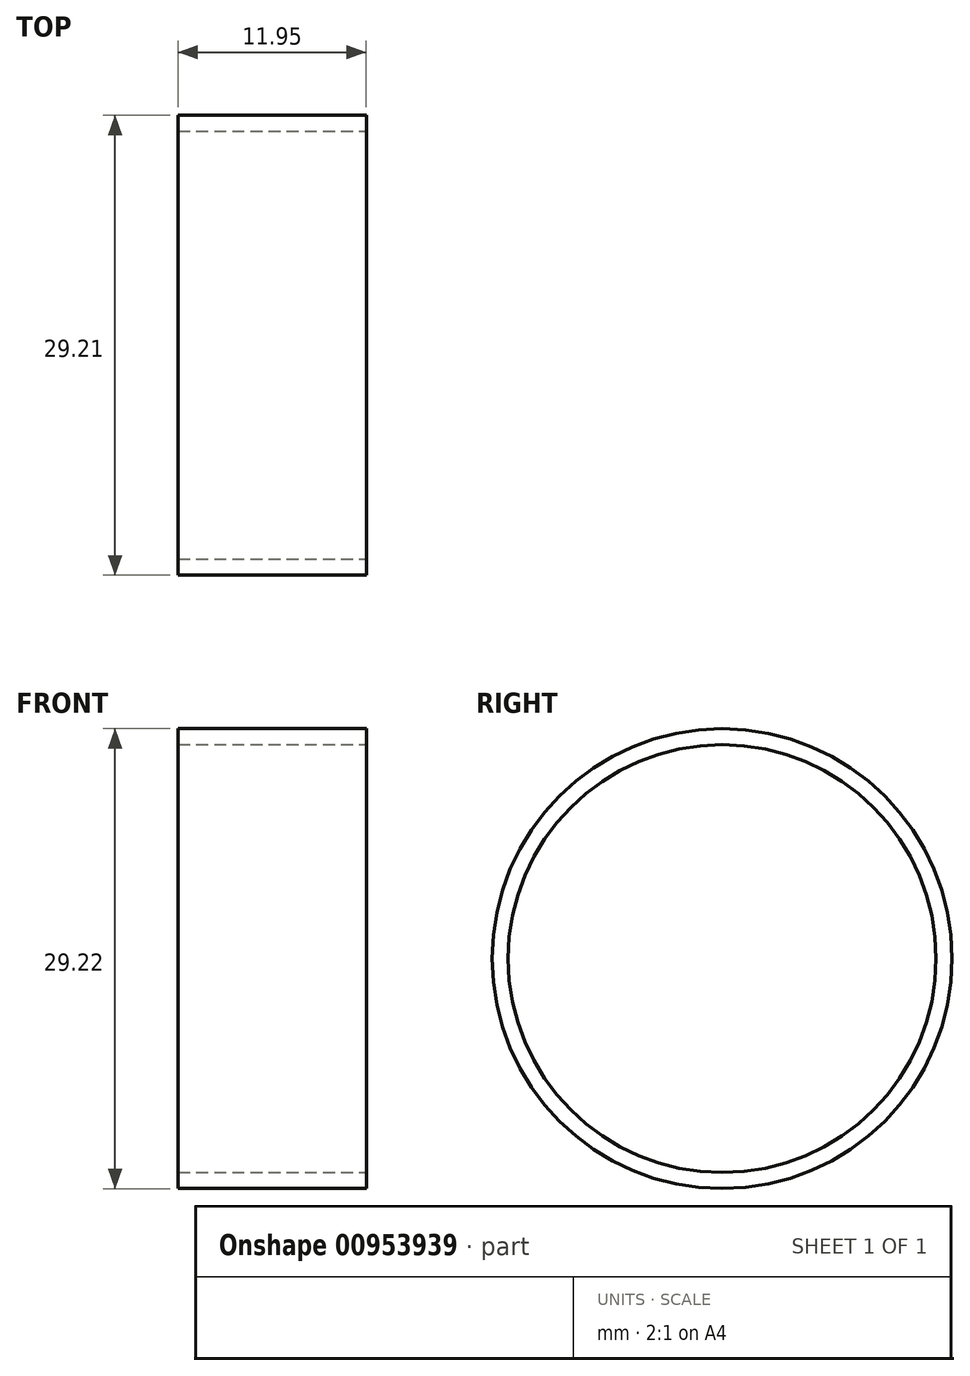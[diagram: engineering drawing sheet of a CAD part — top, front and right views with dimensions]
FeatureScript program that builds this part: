
annotation { "Feature Type Name" : "Feature", "Feature Type Description" : "" }
export const myFeature = defineFeature(function(context is Context, id is Id, definition is map)
    precondition{}
    {
        {
            var Q0;
            Q0=qCreatedBy(makeId("Top.planeOp"),FACE);
            var sketch = newSketch(context, id + "F0", { "sketchPlane" : qUnion([Q0])});
            skLineSegment(sketch, "E0.bottom", {"start": v(-26.7, -2.5) * mm, "end": v(-64.02, -2.5) * mm});
            skLineSegment(sketch, "E0.top", {"start": v(-26.7, -31.7) * mm, "end": v(-64.02, -31.7) * mm});
            skLineSegment(sketch, "E0.left", {"start": v(-26.7, -2.5) * mm, "end": v(-26.7, -31.7) * mm});
            skLineSegment(sketch, "E0.right", {"start": v(-64.02, -2.5) * mm, "end": v(-64.02, -31.7) * mm});
            skLineSegment(sketch, "E1", {"start": v(-26.7, -17.1) * mm, "end": v(-64.02, -17.1) * mm, "construction": true});
            skLineSegment(sketch, "E2.bottom", {"start": v(-64.02, -2.5) * mm, "end": v(-52.07, -2.5) * mm});
            skLineSegment(sketch, "E2.top", {"start": v(-64.02, -3.5) * mm, "end": v(-52.07, -3.5) * mm});
            skLineSegment(sketch, "E2.left", {"start": v(-64.02, -2.5) * mm, "end": v(-64.02, -3.5) * mm});
            skLineSegment(sketch, "E2.right", {"start": v(-52.07, -2.5) * mm, "end": v(-52.07, -3.5) * mm});
            skSolve(sketch);
        }
        {
            var Q0;
            {var subQ4=sQuery(id+"F0.wireOp",EDGE,"E2.top");Q0=makeQuery(id+"F0.imprint","IMPRINT",FACE,{"disambiguationData":[TD([[makeQuery(id+"F0.imprint","IMPRINT",EDGE,{"derivedFrom":subQ4}),1.0]])]});}
            var Q1;
            Q1=sQuery(id+"F0.wireOp",EDGE,"E1");
            revolve(context, id + "F1", {"surfaceOperationType" : NewSurfaceOperationType.NEW, "entities" : qUnion([Q0]), "axis" : qUnion([Q1]), "revolveType" : RevolveType.FULL});
        }
    });
